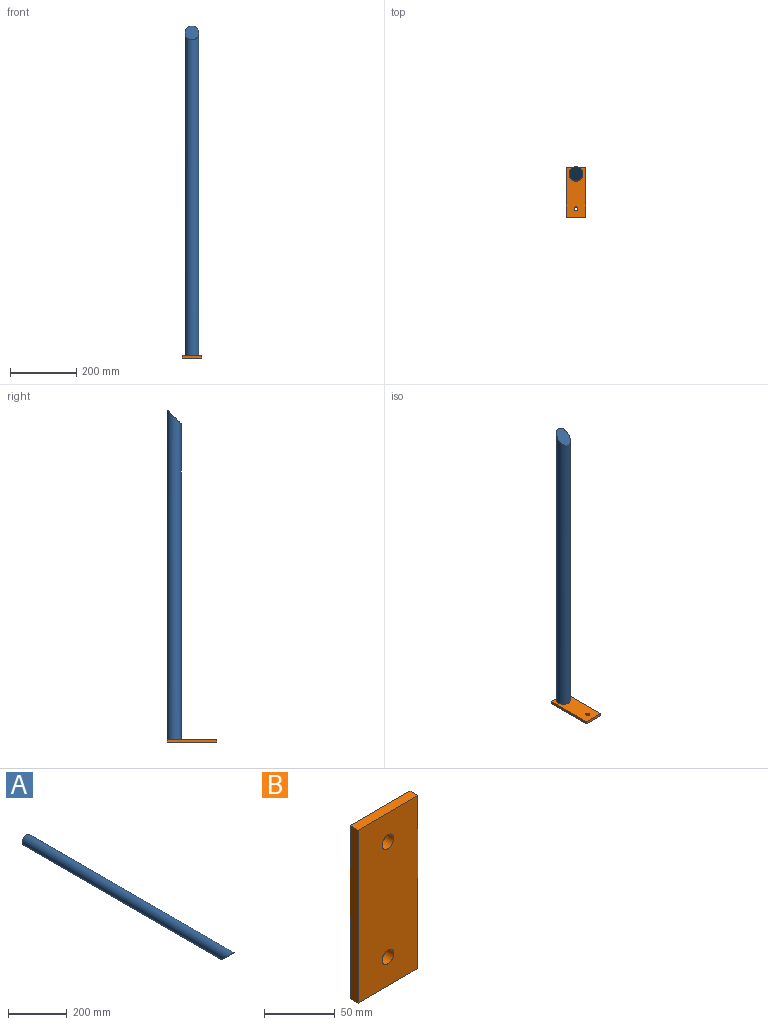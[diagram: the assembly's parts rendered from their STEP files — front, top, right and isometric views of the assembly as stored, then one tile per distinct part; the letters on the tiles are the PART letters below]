
ASSEMBLY  parts=2 mates=1
PART A: 3 faces, bbox 42x992x42 mm
  f0: plane 42x42mm, normal (0,1,0), area 1385.4mm2, adj f2
  f1: plane 42x42mm, normal (0,-0.71,-0.71), area 1959.3mm2, adj f2
  f2: cylinder r=21mm len=992.01mm, axis (0,1,0), area 128120.5mm2, adj f0,f1
PART B: 8 faces, bbox 60x8x150 mm
  f0: plane 60x8mm, normal (0,0,-1), area 480mm2, adj f1,f5,f6,f7
  f1: plane 150x8mm, normal (1,0,0), area 1200mm2, adj f0,f2,f6,f7
  f2: plane 60x8mm, normal (0,0,1), area 480mm2, adj f1,f5,f6,f7
  f3: cylinder r=6mm len=12mm, axis (0,1,0), area 301.6mm2, adj f6,f7
  f4: cylinder r=6mm len=12mm, axis (0,1,0), area 301.6mm2, adj f6,f7
  f5: plane 150x8mm, normal (-1,0,0), area 1200mm2, adj f0,f2,f6,f7
  f6: plane 150x60mm, normal (0,-1,0), area 8773.8mm2, adj f0,f1,f2,f3,f4,f5
  f7: plane 150x60mm, normal (0,1,0), area 8773.8mm2, adj f0,f1,f2,f3,f4,f5
PLACE A rot(axis=(-1,0,0),90deg) t=(206.34,-223.56,-414.39)mm
PLACE B rot(axis=(-1,0,0),90deg) t=(206.34,-277.56,-418.39)mm
MATE fastened B.f6 <-> A.f0  axis (0,0,1) through (206.34,-202.56,-414.39)mm
